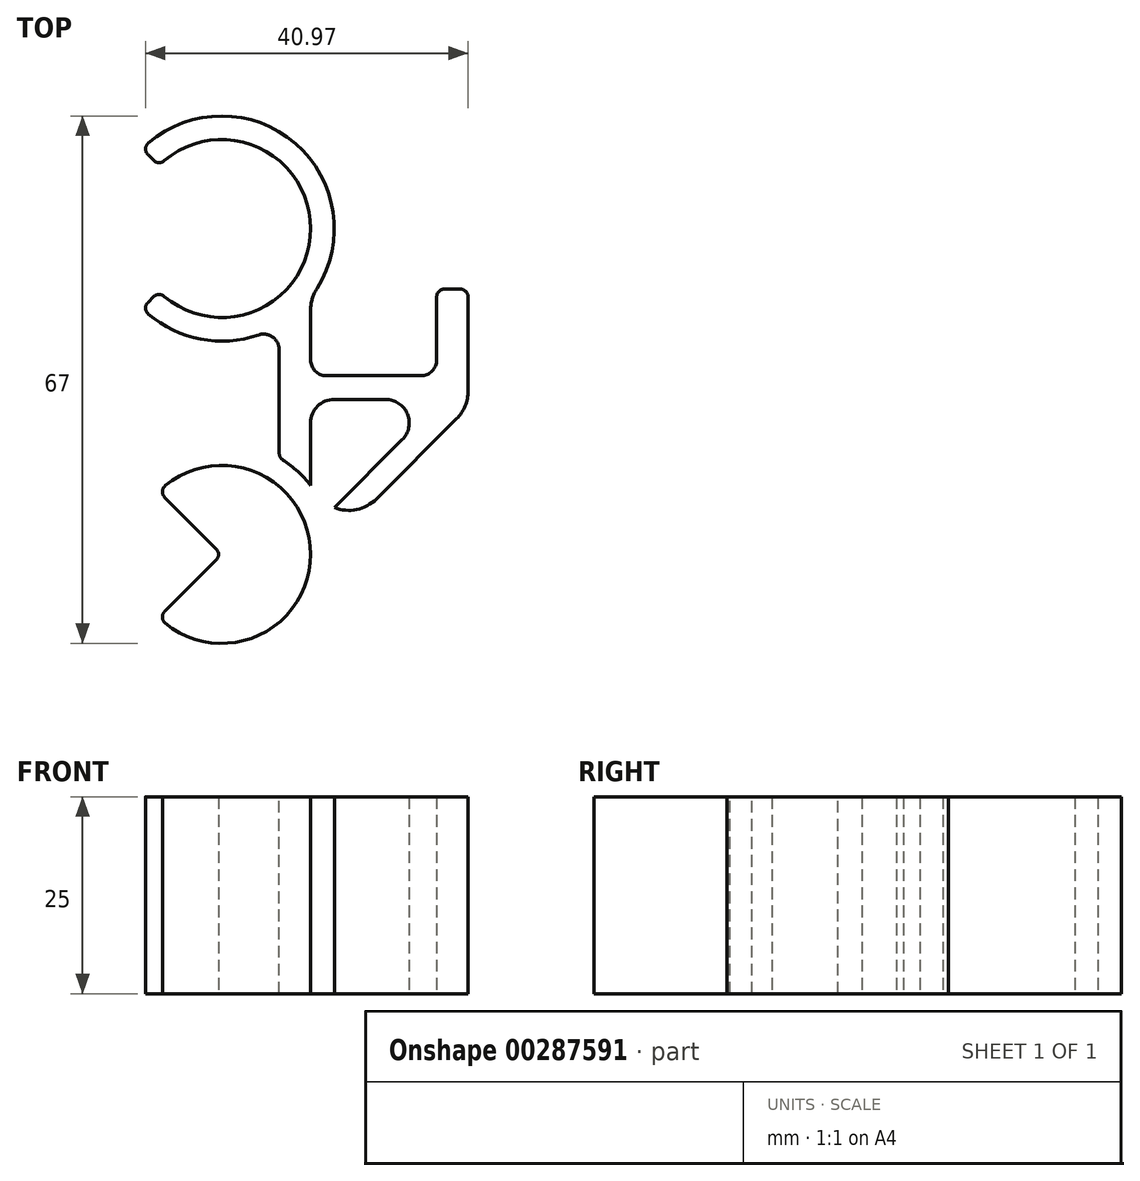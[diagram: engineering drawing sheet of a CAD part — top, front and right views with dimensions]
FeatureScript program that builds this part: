
annotation { "Feature Type Name" : "Feature", "Feature Type Description" : "" }
export const myFeature = defineFeature(function(context is Context, id is Id, definition is map)
    precondition{}
    {
        {
            var Q0;
            Q0=qCreatedBy(makeId("Top.planeOp"),FACE);
            var sketch = newSketch(context, id + "F0", { "sketchPlane" : qUnion([Q0])});
            skLineSegment(sketch, "E0", {"start": v(0, 20.7) * mm, "end": v(0, -20.7) * mm, "construction": true});
            skPoint(sketch, "E1", {"position": v(0, 0) * mm});
            skCircle(sketch, "E2", {"center": v(0, 20.7) * mm, "radius": 11.3 * mm});
            skCircle(sketch, "E3.MirrorC", {"center": v(0, -20.7) * mm, "radius": 11.3 * mm});
            skLineSegment(sketch, "E4", {"start": v(7.3, 12.07) * mm, "end": v(7.3, -12.07) * mm});
            skLineSegment(sketch, "E5", {"start": v(11.3, 20.7) * mm, "end": v(11.3, -20.7) * mm});
            skCircle(sketch, "E6", {"center": v(0, 20.7) * mm, "radius": 14.3 * mm});
            skCircle(sketch, "E7.MirrorC", {"center": v(0, -20.7) * mm, "radius": 14.3 * mm});
            skLineSegment(sketch, "E8", {"start": v(0, 20.7) * mm, "end": v(-10.11, 30.81) * mm});
            skLineSegment(sketch, "E9", {"start": v(0, 20.7) * mm, "end": v(-10.11, 10.59) * mm});
            skLineSegment(sketch, "E10.MirrorCS", {"start": v(0, -20.7) * mm, "end": v(-10.11, -30.81) * mm});
            skLineSegment(sketch, "E11.MirrorCS", {"start": v(0, -20.7) * mm, "end": v(-10.11, -10.59) * mm});
            skLineSegment(sketch, "E12", {"start": v(11.3, -2) * mm, "end": v(31.3, -2) * mm});
            skLineSegment(sketch, "E13", {"start": v(31.3, -2) * mm, "end": v(31.3, 13) * mm});
            skLineSegment(sketch, "E14", {"start": v(31.3, 13) * mm, "end": v(27.3, 13) * mm});
            skLineSegment(sketch, "E15", {"start": v(27.3, 13) * mm, "end": v(27.3, 2) * mm});
            skLineSegment(sketch, "E16", {"start": v(27.3, 2) * mm, "end": v(11.3, 2) * mm});
            skSolve(sketch);
        }
        {
            var Q0;
            {var subQ0=sQuery(id+"F0.wireOp",EDGE,"E4");var subQ1=sQuery(id+"F0.wireOp",EDGE,"E3.MirrorC");var subQ2=makeQuery(id+"F0.imprint","INTERSECT",VERTEX,{"derivedFrom":[subQ1,subQ0]});Q0=makeQuery(id+"F0.imprint","IMPRINT",FACE,{"disambiguationData":[TD([[makeQuery(id+"F0.imprint","IMPRINT",EDGE,{"disambiguationData":[TD([[subQ2,-1.0]])],"derivedFrom":subQ1}),1.0]])]});}
            var Q1;
            {var subQ0=sQuery(id+"F0.wireOp",EDGE,"E6");var subQ1=sQuery(id+"F0.wireOp",EDGE,"E4");var subQ2=makeQuery(id+"F0.imprint","INTERSECT",VERTEX,{"derivedFrom":[subQ1,subQ0]});Q1=makeQuery(id+"F0.imprint","IMPRINT",FACE,{"disambiguationData":[TD([[makeQuery(id+"F0.imprint","IMPRINT",EDGE,{"disambiguationData":[TD([[subQ2,-1.0]])],"derivedFrom":subQ1}),1.0]])]});}
            var Q2;
            {var subQ0=sQuery(id+"F0.wireOp",EDGE,"E4");var subQ1=sQuery(id+"F0.wireOp",EDGE,"E2");var subQ2=makeQuery(id+"F0.imprint","INTERSECT",VERTEX,{"derivedFrom":[subQ1,subQ0]});Q2=makeQuery(id+"F0.imprint","IMPRINT",FACE,{"disambiguationData":[TD([[makeQuery(id+"F0.imprint","IMPRINT",EDGE,{"disambiguationData":[TD([[subQ2,-1.0]])],"derivedFrom":subQ1}),-1.0]])]});}
            var Q3;
            {var subQ0=sQuery(id+"F0.wireOp",EDGE,"E5");var subQ1=sQuery(id+"F0.wireOp",EDGE,"E2");var subQ2=makeQuery(id+"F0.imprint","INTERSECT",VERTEX,{"derivedFrom":[subQ1,subQ0]});Q3=makeQuery(id+"F0.imprint","IMPRINT",FACE,{"disambiguationData":[TD([[makeQuery(id+"F0.imprint","IMPRINT",EDGE,{"disambiguationData":[TD([[subQ2,-1.0]])],"derivedFrom":subQ1}),-1.0]])]});}
            var Q4;
            {var subQ0=sQuery(id+"F0.wireOp",EDGE,"E4");var subQ1=sQuery(id+"F0.wireOp",EDGE,"E2");var subQ2=makeQuery(id+"F0.imprint","INTERSECT",VERTEX,{"derivedFrom":[subQ1,subQ0]});Q4=makeQuery(id+"F0.imprint","IMPRINT",FACE,{"disambiguationData":[TD([[makeQuery(id+"F0.imprint","IMPRINT",EDGE,{"disambiguationData":[TD([[subQ2,1.0]])],"derivedFrom":subQ1}),-1.0]])]});}
            var Q5;
            {var subQ0=sQuery(id+"F0.wireOp",EDGE,"E4");var subQ1=sQuery(id+"F0.wireOp",EDGE,"E3.MirrorC");var subQ2=makeQuery(id+"F0.imprint","INTERSECT",VERTEX,{"derivedFrom":[subQ1,subQ0]});Q5=makeQuery(id+"F0.imprint","IMPRINT",FACE,{"disambiguationData":[TD([[makeQuery(id+"F0.imprint","IMPRINT",EDGE,{"disambiguationData":[TD([[subQ2,1.0]])],"derivedFrom":subQ1}),1.0]])]});}
            var Q6;
            {var subQ0=sQuery(id+"F0.wireOp",EDGE,"E5");var subQ1=sQuery(id+"F0.wireOp",EDGE,"E3.MirrorC");var subQ2=makeQuery(id+"F0.imprint","INTERSECT",VERTEX,{"derivedFrom":[subQ1,subQ0]});Q6=makeQuery(id+"F0.imprint","IMPRINT",FACE,{"disambiguationData":[TD([[makeQuery(id+"F0.imprint","IMPRINT",EDGE,{"disambiguationData":[TD([[subQ2,-1.0]])],"derivedFrom":subQ1}),1.0]])]});}
            var Q7;
            {var subQ0=sQuery(id+"F0.wireOp",EDGE,"E12");Q7=makeQuery(id+"F0.imprint","IMPRINT",FACE,{"disambiguationData":[TD([[makeQuery(id+"F0.imprint","IMPRINT",EDGE,{"derivedFrom":subQ0}),1.0]])]});}
            extrude(context, id + "F1", {"entities" : qUnion([Q0, Q1, Q2, Q3, Q4, Q5, Q6, Q7]), "depth" : 25 * mm, "offsetDistance" : 25 * mm});
        }
        {
            var Q0;
            Q0=makeQuery(id+"F1.opExtrude","SWEPT_EDGE",EDGE,{"disambiguationData":[OSD([sQuery(id+"F0.wireOp",EDGE,"E5"),sQuery(id+"F0.wireOp",EDGE,"E12")])]});
            chamfer(context, id + "F2", {"entities" : qUnion([Q0]), "width" : 20 * mm, "tangentPropagation" : true});
        }
        {
            var Q0;
            Q0=makeQuery(id+"F1.opExtrude","SWEPT_EDGE",EDGE,{"disambiguationData":[OSD([sQuery(id+"F0.wireOp",EDGE,"E15"),sQuery(id+"F0.wireOp",EDGE,"E16")])]});
            var Q1;
            Q1=makeQuery(id+"F1.opExtrude","SWEPT_EDGE",EDGE,{"disambiguationData":[OSD([sQuery(id+"F0.wireOp",EDGE,"E5"),sQuery(id+"F0.wireOp",EDGE,"E16")])]});
            fillet(context, id + "F3", {"entities" : qUnion([Q0, Q1]), "radius" : 2 * mm, "tangentPropagation" : true, "allowEdgeOverflow" : false});
        }
        {
            var Q0;
            Q0=makeQuery(id+"F1.opExtrude","SWEPT_EDGE",EDGE,{"disambiguationData":[OSD([sQuery(id+"F0.wireOp",EDGE,"E13"),sQuery(id+"F0.wireOp",EDGE,"E14")])]});
            var Q1;
            Q1=makeQuery(id+"F1.opExtrude","SWEPT_EDGE",EDGE,{"disambiguationData":[OSD([sQuery(id+"F0.wireOp",EDGE,"E14"),sQuery(id+"F0.wireOp",EDGE,"E15")])]});
            var Q2;
            Q2=makeQuery(id+"F1.opExtrude","SWEPT_EDGE",EDGE,{"disambiguationData":[OSD([sQuery(id+"F0.wireOp",EDGE,"E3.MirrorC"),sQuery(id+"F0.wireOp",EDGE,"E11.MirrorCS")])]});
            var Q3;
            Q3=makeQuery(id+"F1.opExtrude","SWEPT_EDGE",EDGE,{"disambiguationData":[OSD([sQuery(id+"F0.wireOp",EDGE,"E7.MirrorC"),sQuery(id+"F0.wireOp",EDGE,"E11.MirrorCS")])]});
            var Q4;
            Q4=makeQuery(id+"F1.opExtrude","SWEPT_EDGE",EDGE,{"disambiguationData":[OSD([sQuery(id+"F0.wireOp",EDGE,"E3.MirrorC"),sQuery(id+"F0.wireOp",EDGE,"E10.MirrorCS")])]});
            var Q5;
            Q5=makeQuery(id+"F1.opExtrude","SWEPT_EDGE",EDGE,{"disambiguationData":[OSD([sQuery(id+"F0.wireOp",EDGE,"E7.MirrorC"),sQuery(id+"F0.wireOp",EDGE,"E10.MirrorCS")])]});
            var Q6;
            Q6=makeQuery(id+"F1.opExtrude","SWEPT_EDGE",EDGE,{"disambiguationData":[OSD([sQuery(id+"F0.wireOp",EDGE,"E6"),sQuery(id+"F0.wireOp",EDGE,"E9")])]});
            var Q7;
            Q7=makeQuery(id+"F1.opExtrude","SWEPT_EDGE",EDGE,{"disambiguationData":[OSD([sQuery(id+"F0.wireOp",EDGE,"E2"),sQuery(id+"F0.wireOp",EDGE,"E9")])]});
            var Q8;
            Q8=makeQuery(id+"F1.opExtrude","SWEPT_EDGE",EDGE,{"disambiguationData":[OSD([sQuery(id+"F0.wireOp",EDGE,"E2"),sQuery(id+"F0.wireOp",EDGE,"E8")])]});
            var Q9;
            Q9=makeQuery(id+"F1.opExtrude","SWEPT_EDGE",EDGE,{"disambiguationData":[OSD([sQuery(id+"F0.wireOp",EDGE,"E6"),sQuery(id+"F0.wireOp",EDGE,"E8")])]});
            fillet(context, id + "F4", {"entities" : qUnion([Q0, Q1, Q2, Q3, Q4, Q5, Q6, Q7, Q8, Q9]), "radius" : 1 * mm, "tangentPropagation" : true, "allowEdgeOverflow" : false});
        }
        {
            var Q0;
            Q0=makeQuery(id+"F2.opChamfer","BLEND_EDGE",EDGE,{"blendedFrom":[makeQuery(id+"F1.opExtrude","SWEPT_EDGE",EDGE,{"disambiguationData":[OSD([sQuery(id+"F0.wireOp",EDGE,"E5"),sQuery(id+"F0.wireOp",EDGE,"E12")])]}),makeQuery(id+"F1.opExtrude","SWEPT_FACE",FACE,{"disambiguationData":[OSD([sQuery(id+"F0.wireOp",EDGE,"E13")])]})],"blendedInto":[makeQuery(id+"F1.opExtrude","SWEPT_FACE",FACE,{"disambiguationData":[OSD([sQuery(id+"F0.wireOp",EDGE,"E13")])]})]});
            var Q1;
            {var subQ0=sQuery(id+"F0.wireOp",EDGE,"E7.MirrorC");var subQ1=sQuery(id+"F0.wireOp",EDGE,"E5");Q1=makeQuery(id+"F2.opChamfer","BLEND_EDGE",EDGE,{"blendedFrom":[makeQuery(id+"F1.opExtrude","SWEPT_EDGE",EDGE,{"disambiguationData":[OSD([subQ1,sQuery(id+"F0.wireOp",EDGE,"E12")])]}),makeQuery(id+"F1.opExtrude","SWEPT_FACE",FACE,{"disambiguationData":[OSD([subQ0]),TDD([makeQuery(id+"F0.imprint","IMPRINT",EDGE,{"disambiguationData":[TD([[makeQuery(id+"F0.imprint","INTERSECT",VERTEX,{"derivedFrom":[subQ0,sQuery(id+"F0.wireOp",EDGE,"E10.MirrorCS")]}),1.0]])],"derivedFrom":subQ0})])]})],"blendedInto":[makeQuery(id+"F1.opExtrude","SWEPT_FACE",FACE,{"disambiguationData":[OSD([subQ0]),TDD([makeQuery(id+"F0.imprint","IMPRINT",EDGE,{"disambiguationData":[TD([[makeQuery(id+"F0.imprint","INTERSECT",VERTEX,{"derivedFrom":[subQ0,sQuery(id+"F0.wireOp",EDGE,"E10.MirrorCS")]}),1.0]])],"derivedFrom":subQ0})])]})]});}
            var Q2;
            Q2=makeQuery(id+"F1.opExtrude","SWEPT_EDGE",EDGE,{"disambiguationData":[OSD([sQuery(id+"F0.wireOp",EDGE,"E5"),sQuery(id+"F0.wireOp",EDGE,"E6")])]});
            fillet(context, id + "F5", {"entities" : qUnion([Q0, Q1, Q2]), "radius" : 5 * mm, "tangentPropagation" : true, "allowEdgeOverflow" : false});
        }
        {
            var Q0;
            Q0=makeQuery(id+"F1.opExtrude","SWEPT_EDGE",EDGE,{"disambiguationData":[OSD([sQuery(id+"F0.wireOp",EDGE,"E4"),sQuery(id+"F0.wireOp",EDGE,"E6")])]});
            var Q1;
            Q1=makeQuery(id+"F1.opExtrude","SWEPT_EDGE",EDGE,{"disambiguationData":[OSD([sQuery(id+"F0.wireOp",EDGE,"E4"),sQuery(id+"F0.wireOp",EDGE,"E7.MirrorC")])]});
            fillet(context, id + "F6", {"entities" : qUnion([Q0, Q1]), "radius" : 2 * mm, "tangentPropagation" : true, "allowEdgeOverflow" : false});
        }
        {
            var Q0;
            Q0=makeQuery(id+"F1.opExtrude","CAP_FACE",FACE,{"disambiguationData":[OSD([sQuery(id+"F0.wireOp",EDGE,"E2"),sQuery(id+"F0.wireOp",EDGE,"E3.MirrorC"),sQuery(id+"F0.wireOp",EDGE,"E4"),sQuery(id+"F0.wireOp",EDGE,"E5"),sQuery(id+"F0.wireOp",EDGE,"E6"),sQuery(id+"F0.wireOp",EDGE,"E7.MirrorC"),sQuery(id+"F0.wireOp",EDGE,"E8"),sQuery(id+"F0.wireOp",EDGE,"E9"),sQuery(id+"F0.wireOp",EDGE,"E10.MirrorCS"),sQuery(id+"F0.wireOp",EDGE,"E11.MirrorCS"),sQuery(id+"F0.wireOp",EDGE,"E12"),sQuery(id+"F0.wireOp",EDGE,"E13"),sQuery(id+"F0.wireOp",EDGE,"E14"),sQuery(id+"F0.wireOp",EDGE,"E15"),sQuery(id+"F0.wireOp",EDGE,"E16")])],"isStart":false});
            var sketch = newSketch(context, id + "F7", { "sketchPlane" : qUnion([Q0])});
            skLineSegment(sketch, "E17", {"start": v(11.3, -1) * mm, "end": v(28.06, -1) * mm});
            skLineSegment(sketch, "E18", {"start": v(28.06, -1) * mm, "end": v(11.3, -17.76) * mm});
            skLineSegment(sketch, "E19", {"start": v(11.3, -17.76) * mm, "end": v(11.3, -1) * mm});
            skSolve(sketch);
        }
        {
            var Q0;
            Q0=makeQuery(id+"F7.imprint","IMPRINT",FACE,{"disambiguationData":[TD([[makeQuery(id+"F7.imprint","IMPRINT",EDGE,{"derivedFrom":sQuery(id+"F7.wireOp",EDGE,"E17")}),-1.0]])]});
            extrude(context, id + "F8", {"entities" : qUnion([Q0]), "operationType" : NewBodyOperationType.REMOVE, "endBound" : BoundingType.THROUGH_ALL, "oppositeDirection" : true, "depth" : 25 * mm, "offsetDistance" : 25 * mm});
        }
        {
            var Q0;
            Q0=makeQuery(id+"F8.boolean.opBoolean","COPY",EDGE,{"derivedFrom":makeQuery(id+"F8.opExtrude","SWEPT_EDGE",EDGE,{"disambiguationData":[OSD([sQuery(id+"F7.wireOp",EDGE,"E17"),sQuery(id+"F7.wireOp",EDGE,"E19")])]})});
            var Q1;
            Q1=makeQuery(id+"F8.boolean.opBoolean","COPY",EDGE,{"derivedFrom":makeQuery(id+"F8.opExtrude","SWEPT_EDGE",EDGE,{"disambiguationData":[OSD([sQuery(id+"F7.wireOp",EDGE,"E17"),sQuery(id+"F7.wireOp",EDGE,"E18")])]})});
            var Q2;
            Q2=makeQuery(id+"F8.boolean.opBoolean","COPY",EDGE,{"derivedFrom":makeQuery(id+"F8.opExtrude","SWEPT_EDGE",EDGE,{"disambiguationData":[OSD([sQuery(id+"F7.wireOp",EDGE,"E18"),sQuery(id+"F7.wireOp",EDGE,"E19")])]})});
            fillet(context, id + "F9", {"entities" : qUnion([Q0, Q1, Q2]), "radius" : 3 * mm, "tangentPropagation" : true, "allowEdgeOverflow" : false});
        }
    });
